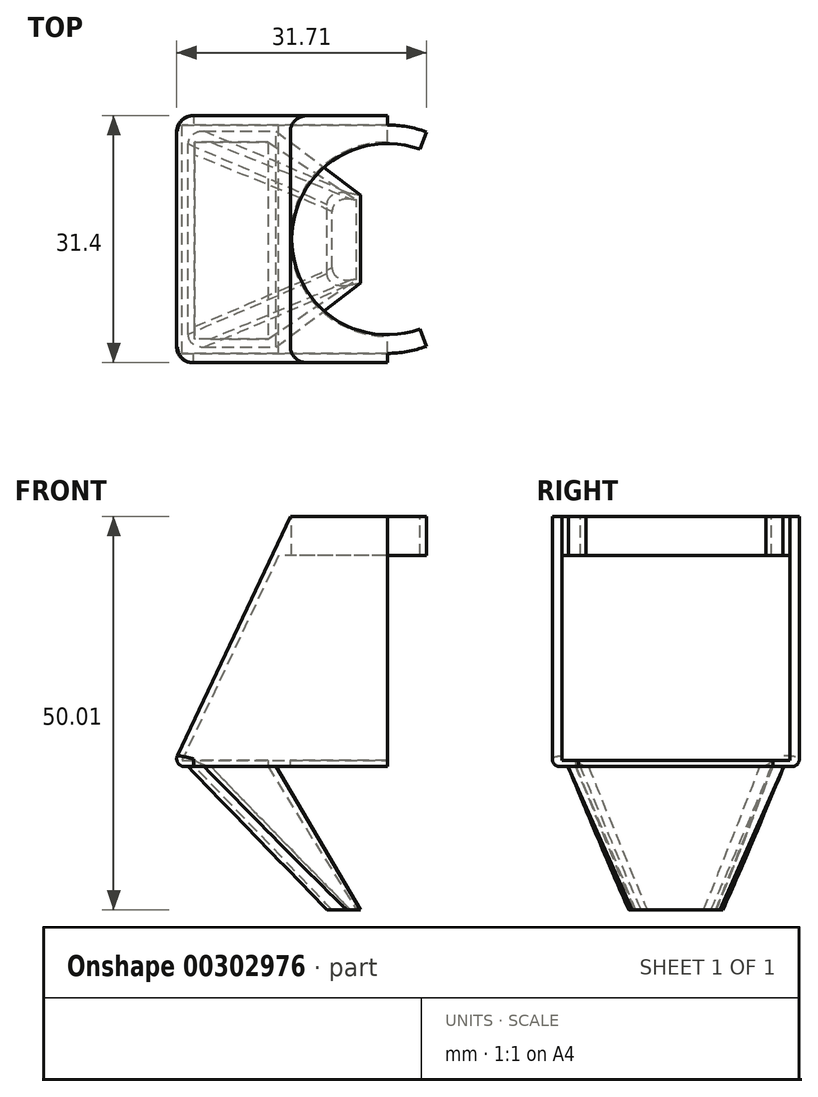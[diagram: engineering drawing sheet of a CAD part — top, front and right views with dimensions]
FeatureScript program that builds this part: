
annotation { "Feature Type Name" : "Feature", "Feature Type Description" : "" }
export const myFeature = defineFeature(function(context is Context, id is Id, definition is map)
    precondition{}
    {
        {
            var Q0;
            Q0=qCreatedBy(makeId("Front.planeOp"),FACE);
            var sketch = newSketch(context, id + "F0", { "sketchPlane" : qUnion([Q0])});
            skLineSegment(sketch, "E0.bottom", {"start": v(12.33, 15.9) * mm, "end": v(-12.33, 15.9) * mm, "construction": true});
            skLineSegment(sketch, "E0.top", {"start": v(12.32, -15.9) * mm, "end": v(-12.33, -15.9) * mm, "construction": true});
            skLineSegment(sketch, "E0.left", {"start": v(12.33, 15.9) * mm, "end": v(12.32, -15.9) * mm, "construction": true});
            skLineSegment(sketch, "E0.right", {"start": v(-12.33, 15.9) * mm, "end": v(-12.33, -15.9) * mm, "construction": true});
            skPoint(sketch, "E0.middle", {"position": v(0, 0) * mm});
            skLineSegment(sketch, "E1", {"start": v(-12.33, 15.9) * mm, "end": v(-27.33, -15.9) * mm});
            skLineSegment(sketch, "E2", {"start": v(-27.33, -15.9) * mm, "end": v(-12.33, -15.9) * mm});
            skLineSegment(sketch, "E3", {"start": v(-13.8, 10.9) * mm, "end": v(-26.06, -15.1) * mm});
            skLineSegment(sketch, "E4", {"start": v(-12.33, -15.1) * mm, "end": v(-26.06, -15.1) * mm});
            skLineSegment(sketch, "E5", {"start": v(-12.33, 15.9) * mm, "end": v(0, 15.9) * mm});
            skLineSegment(sketch, "E6", {"start": v(0, 15.9) * mm, "end": v(0, 10.9) * mm});
            skLineSegment(sketch, "E7", {"start": v(0, 10.9) * mm, "end": v(-13.8, 10.9) * mm});
            skLineSegment(sketch, "E8", {"start": v(-12.33, -15.1) * mm, "end": v(0, -15.1) * mm});
            skLineSegment(sketch, "E9", {"start": v(0, -15.1) * mm, "end": v(0, -15.9) * mm});
            skLineSegment(sketch, "E10", {"start": v(0, -15.9) * mm, "end": v(-12.33, -15.9) * mm});
            skSolve(sketch);
        }
        {
            var Q0;
            Q0=makeQuery(id+"F0.imprint","IMPRINT",FACE,{"disambiguationData":[TD([[makeQuery(id+"F0.imprint","IMPRINT",EDGE,{"derivedFrom":sQuery(id+"F0.wireOp",EDGE,"E1")}),1.0]])]});
            extrude(context, id + "F1", {"entities" : qUnion([Q0]), "endBound" : BoundingType.SYMMETRIC, "depth" : 29 * mm, "offsetDistance" : 25 * mm});
        }
        {
            var Q0;
            Q0=makeQuery(id+"F1.opExtrude","SWEPT_FACE",FACE,{"disambiguationData":[OSD([sQuery(id+"F0.wireOp",EDGE,"E5")])]});
            var sketch = newSketch(context, id + "F2", { "sketchPlane" : qUnion([Q0])});
            skCircle(sketch, "E11", {"center": v(0, 0) * mm, "radius": 12.15 * mm});
            skCircle(sketch, "E12", {"center": v(0, 0) * mm, "radius": 14.5 * mm});
            skLineSegment(sketch, "E13", {"start": v(0, 0) * mm, "end": v(4.96, 13.63) * mm});
            skLineSegment(sketch, "E14", {"start": v(0, 0) * mm, "end": v(4.96, -13.63) * mm});
            skSolve(sketch);
        }
        {
            var Q0;
            {var subQ0=sQuery(id+"F0.wireOp",EDGE,"E5");var subQ1=makeQuery(id+"F1.opExtrude","SWEPT_EDGE",EDGE,{"disambiguationData":[OSD([subQ0,sQuery(id+"F0.wireOp",EDGE,"E6")])]});var subQ3=sQuery(id+"F2.wireOp",EDGE,"E11");var subQ4=makeQuery(id+"F2.imprint","INTERSECT",VERTEX,{"disambiguationData":[OD(0.0)],"derivedFrom":[subQ1,subQ3]});Q0=makeQuery(id+"F2.imprint","IMPRINT",FACE,{"disambiguationData":[TD([[makeQuery(id+"F2.imprint","IMPRINT",EDGE,{"disambiguationData":[TD([[subQ4,-1.0]])],"derivedFrom":subQ3}),1.0]])]});}
            extrude(context, id + "F3", {"entities" : qUnion([Q0]), "operationType" : NewBodyOperationType.REMOVE, "oppositeDirection" : true, "depth" : 6 * mm, "offsetDistance" : 25 * mm});
        }
        {
            var Q0;
            {var subQ0=sQuery(id+"F2.wireOp",EDGE,"E13");var subQ6=sQuery(id+"F2.wireOp",EDGE,"E12");var subQ8=makeQuery(id+"F2.imprint","INTERSECT",VERTEX,{"derivedFrom":[subQ6,subQ0]});Q0=makeQuery(id+"F2.imprint","IMPRINT",FACE,{"disambiguationData":[TD([[makeQuery(id+"F2.imprint","IMPRINT",EDGE,{"disambiguationData":[TD([[subQ8,1.0]])],"derivedFrom":subQ0}),1.0]])]});}
            var Q1;
            {var subQ0=sQuery(id+"F2.wireOp",EDGE,"E14");var subQ6=sQuery(id+"F2.wireOp",EDGE,"E12");var subQ8=makeQuery(id+"F2.imprint","INTERSECT",VERTEX,{"derivedFrom":[subQ6,subQ0]});Q1=makeQuery(id+"F2.imprint","IMPRINT",FACE,{"disambiguationData":[TD([[makeQuery(id+"F2.imprint","IMPRINT",EDGE,{"disambiguationData":[TD([[subQ8,1.0]])],"derivedFrom":subQ0}),-1.0]])]});}
            extrude(context, id + "F4", {"entities" : qUnion([Q0, Q1]), "operationType" : NewBodyOperationType.ADD, "oppositeDirection" : true, "depth" : 5 * mm, "offsetDistance" : 25 * mm});
        }
        {
            var Q0;
            Q0=makeQuery(id+"F1.opExtrude","CAP_FACE",FACE,{"disambiguationData":[OSD([sQuery(id+"F0.wireOp",EDGE,"E1"),sQuery(id+"F0.wireOp",EDGE,"E2"),sQuery(id+"F0.wireOp",EDGE,"E3"),sQuery(id+"F0.wireOp",EDGE,"E4"),sQuery(id+"F0.wireOp",EDGE,"E5"),sQuery(id+"F0.wireOp",EDGE,"E6"),sQuery(id+"F0.wireOp",EDGE,"E7"),sQuery(id+"F0.wireOp",EDGE,"E8"),sQuery(id+"F0.wireOp",EDGE,"E9"),sQuery(id+"F0.wireOp",EDGE,"E10")])],"isStart":false});
            var sketch = newSketch(context, id + "F5", { "sketchPlane" : qUnion([Q0])});
            skLineSegment(sketch, "E15", {"start": v(0, 15.9) * mm, "end": v(0, -15.9) * mm});
            skSolve(sketch);
        }
        {
            var Q0;
            Q0=makeQuery(id+"F5.imprint","IMPRINT",FACE,{"disambiguationData":[TD([[makeQuery(id+"F5.imprint","IMPRINT",EDGE,{"derivedFrom":makeQuery(id+"F1.opExtrude","CAP_EDGE",EDGE,{"disambiguationData":[OSD([sQuery(id+"F0.wireOp",EDGE,"E1")])],"isStart":false})}),1.0]])]});
            var Q1;
            Q1=makeQuery(id+"F5.imprint","IMPRINT",FACE,{"disambiguationData":[TD([[makeQuery(id+"F5.imprint","IMPRINT",EDGE,{"derivedFrom":makeQuery(id+"F1.opExtrude","CAP_EDGE",EDGE,{"disambiguationData":[OSD([sQuery(id+"F0.wireOp",EDGE,"E3")])],"isStart":false})}),1.0]])]});
            extrude(context, id + "F6", {"entities" : qUnion([Q0, Q1]), "operationType" : NewBodyOperationType.ADD, "depth" : 1.2 * mm, "offsetDistance" : 25 * mm});
        }
        {
            var Q0;
            Q0=makeQuery(id+"F1.opExtrude","CAP_FACE",FACE,{"disambiguationData":[OSD([sQuery(id+"F0.wireOp",EDGE,"E1"),sQuery(id+"F0.wireOp",EDGE,"E2"),sQuery(id+"F0.wireOp",EDGE,"E3"),sQuery(id+"F0.wireOp",EDGE,"E4"),sQuery(id+"F0.wireOp",EDGE,"E5"),sQuery(id+"F0.wireOp",EDGE,"E6"),sQuery(id+"F0.wireOp",EDGE,"E7"),sQuery(id+"F0.wireOp",EDGE,"E8"),sQuery(id+"F0.wireOp",EDGE,"E9"),sQuery(id+"F0.wireOp",EDGE,"E10")])],"isStart":true});
            var sketch = newSketch(context, id + "F7", { "sketchPlane" : qUnion([Q0])});
            skLineSegment(sketch, "E16", {"start": v(0, 15.9) * mm, "end": v(0, -15.9) * mm});
            skSolve(sketch);
        }
        {
            var Q0;
            Q0=makeQuery(id+"F7.imprint","IMPRINT",FACE,{"disambiguationData":[TD([[makeQuery(id+"F7.imprint","IMPRINT",EDGE,{"derivedFrom":makeQuery(id+"F1.opExtrude","CAP_EDGE",EDGE,{"disambiguationData":[OSD([sQuery(id+"F0.wireOp",EDGE,"E1")])],"isStart":true})}),-1.0]])]});
            var Q1;
            Q1=makeQuery(id+"F7.imprint","IMPRINT",FACE,{"disambiguationData":[TD([[makeQuery(id+"F7.imprint","IMPRINT",EDGE,{"derivedFrom":makeQuery(id+"F1.opExtrude","CAP_EDGE",EDGE,{"disambiguationData":[OSD([sQuery(id+"F0.wireOp",EDGE,"E3")])],"isStart":true})}),-1.0]])]});
            extrude(context, id + "F8", {"entities" : qUnion([Q0, Q1]), "operationType" : NewBodyOperationType.ADD, "depth" : 1.2 * mm, "offsetDistance" : 25 * mm});
        }
        {
            var Q0;
            {var subQ0=sQuery(id+"F0.wireOp",EDGE,"E10");var subQ1=sQuery(id+"F0.wireOp",EDGE,"E2");Q0=makeQuery(id+"F8.boolean.opBoolean","MERGE",FACE,{"derivedFrom":[makeQuery(id+"F6.boolean.opBoolean","MERGE",FACE,{"derivedFrom":[makeQuery(id+"F1.opExtrude","SWEPT_FACE",FACE,{"disambiguationData":[OSD([subQ1,subQ0])]}),makeQuery(id+"F6.opExtrude","SWEPT_FACE",FACE,{"disambiguationData":[OSD([subQ1,subQ0])]})]}),makeQuery(id+"F8.opExtrude","SWEPT_FACE",FACE,{"disambiguationData":[OSD([subQ1,subQ0])]})]});}
            var sketch = newSketch(context, id + "F9", { "sketchPlane" : qUnion([Q0])});
            skCircle(sketch, "E17", {"center": v(0, 0) * mm, "radius": 12.35 * mm});
            skSolve(sketch);
        }
        {
            var Q0;
            {var subQ0=sQuery(id+"F9.wireOp",EDGE,"E17");var subQ1=sQuery(id+"F0.wireOp",EDGE,"E10");var subQ2=sQuery(id+"F0.wireOp",EDGE,"E2");var subQ3=makeQuery(id+"F8.boolean.opBoolean","MERGE",EDGE,{"derivedFrom":[makeQuery(id+"F6.boolean.opBoolean","MERGE",EDGE,{"derivedFrom":[makeQuery(id+"F1.opExtrude","SWEPT_EDGE",EDGE,{"disambiguationData":[OSD([sQuery(id+"F0.wireOp",EDGE,"E9"),subQ1])]}),makeQuery(id+"F6.opExtrude","SWEPT_EDGE",EDGE,{"disambiguationData":[OSD([subQ2,subQ1,sQuery(id+"F5.wireOp",EDGE,"E15")])]})]}),makeQuery(id+"F8.opExtrude","SWEPT_EDGE",EDGE,{"disambiguationData":[OSD([subQ2,subQ1,sQuery(id+"F7.wireOp",EDGE,"E16")])]})]});var subQ4=makeQuery(id+"F9.imprint","INTERSECT",VERTEX,{"disambiguationData":[OD(0.0)],"derivedFrom":[subQ3,subQ0]});Q0=makeQuery(id+"F9.imprint","IMPRINT",FACE,{"disambiguationData":[TD([[makeQuery(id+"F9.imprint","IMPRINT",EDGE,{"disambiguationData":[TD([[subQ4,-1.0]])],"derivedFrom":subQ0}),1.0]])]});}
            extrude(context, id + "F10", {"entities" : qUnion([Q0]), "operationType" : NewBodyOperationType.REMOVE, "oppositeDirection" : true, "depth" : 2 * mm, "offsetDistance" : 25 * mm});
        }
        {
            var Q0;
            {var subQ0=sQuery(id+"F0.wireOp",EDGE,"E10");var subQ1=sQuery(id+"F0.wireOp",EDGE,"E2");Q0=makeQuery(id+"F8.boolean.opBoolean","MERGE",FACE,{"derivedFrom":[makeQuery(id+"F6.boolean.opBoolean","MERGE",FACE,{"derivedFrom":[makeQuery(id+"F1.opExtrude","SWEPT_FACE",FACE,{"disambiguationData":[OSD([subQ1,subQ0])]}),makeQuery(id+"F6.opExtrude","SWEPT_FACE",FACE,{"disambiguationData":[OSD([subQ1,subQ0])]})]}),makeQuery(id+"F8.opExtrude","SWEPT_FACE",FACE,{"disambiguationData":[OSD([subQ1,subQ0])]})]});}
            var sketch = newSketch(context, id + "F11", { "sketchPlane" : qUnion([Q0])});
            skLineSegment(sketch, "E18.bottom", {"start": v(-25.32, 13.7) * mm, "end": v(-14.15, 13.7) * mm});
            skLineSegment(sketch, "E18.top", {"start": v(-25.32, -13.7) * mm, "end": v(-14.15, -13.7) * mm});
            skLineSegment(sketch, "E18.left", {"start": v(-25.32, 13.7) * mm, "end": v(-25.32, -13.7) * mm});
            skLineSegment(sketch, "E18.right", {"start": v(-14.15, 13.7) * mm, "end": v(-14.15, -13.7) * mm});
            skSolve(sketch);
        }
        {
            var Q0;
            Q0=makeQuery(id+"F11.imprint","IMPRINT",FACE,{"disambiguationData":[TD([[makeQuery(id+"F11.imprint","IMPRINT",EDGE,{"derivedFrom":sQuery(id+"F11.wireOp",EDGE,"E18.bottom")}),1.0]])]});
            var sketch = newSketch(context, id + "F12", { "sketchPlane" : qUnion([Q0])});
            skLineSegment(sketch, "E19.bottom", {"start": v(-24.47, 12.69) * mm, "end": v(-15.17, 12.69) * mm});
            skLineSegment(sketch, "E19.top", {"start": v(-24.47, -12.3) * mm, "end": v(-15.17, -12.3) * mm});
            skLineSegment(sketch, "E19.left", {"start": v(-24.47, 12.69) * mm, "end": v(-24.47, -12.3) * mm});
            skLineSegment(sketch, "E19.right", {"start": v(-15.17, 12.69) * mm, "end": v(-15.17, -12.3) * mm});
            skSolve(sketch);
        }
        {
            var Q0;
            Q0=makeQuery(id+"F12.imprint","IMPRINT",FACE,{"disambiguationData":[TD([[makeQuery(id+"F12.imprint","IMPRINT",EDGE,{"derivedFrom":sQuery(id+"F12.wireOp",EDGE,"E19.bottom")}),-1.0]])]});
            extrude(context, id + "F13", {"entities" : qUnion([Q0]), "operationType" : NewBodyOperationType.REMOVE, "oppositeDirection" : true, "depth" : 2 * mm, "offsetDistance" : 25 * mm});
        }
        {
            var Q0;
            {var subQ0=sQuery(id+"F5.wireOp",EDGE,"E15");var subQ2=sQuery(id+"F0.wireOp",EDGE,"E5");Q0=makeQuery(id+"F10.boolean.opBoolean","SPLIT",FACE,{"disambiguationData":[TD([makeQuery(id+"F6.opExtrude","SWEPT_FACE",FACE,{"disambiguationData":[OSD([subQ2])]})])],"derivedFrom":makeQuery(id+"F8.boolean.opBoolean","MERGE",FACE,{"derivedFrom":[makeQuery(id+"F6.boolean.opBoolean","MERGE",FACE,{"derivedFrom":[makeQuery(id+"F1.opExtrude","SWEPT_FACE",FACE,{"disambiguationData":[OSD([sQuery(id+"F0.wireOp",EDGE,"E9")])]}),makeQuery(id+"F6.opExtrude","SWEPT_FACE",FACE,{"disambiguationData":[OSD([subQ0])]})]}),makeQuery(id+"F8.opExtrude","SWEPT_FACE",FACE,{"disambiguationData":[OSD([sQuery(id+"F7.wireOp",EDGE,"E16")])]})]})});}
            var sketch = newSketch(context, id + "F14", { "sketchPlane" : qUnion([Q0])});
            skLineSegment(sketch, "E20", {"start": v(-15.7, -15.9) * mm, "end": v(0, -15.9) * mm, "construction": true});
            skLineSegment(sketch, "E21", {"start": v(0, -15.9) * mm, "end": v(0, 0) * mm, "construction": true});
            skLineSegment(sketch, "E22", {"start": v(0, -15.9) * mm, "end": v(0, -40.9) * mm, "construction": true});
            skLineSegment(sketch, "E23.bottom", {"start": v(2.5, -40.4) * mm, "end": v(-2.5, -40.4) * mm});
            skLineSegment(sketch, "E23.top", {"start": v(2.5, -41.4) * mm, "end": v(-2.5, -41.4) * mm});
            skLineSegment(sketch, "E23.left", {"start": v(2.5, -40.4) * mm, "end": v(2.5, -41.4) * mm});
            skLineSegment(sketch, "E23.right", {"start": v(-2.5, -40.4) * mm, "end": v(-2.5, -41.4) * mm});
            skPoint(sketch, "E23.middle", {"position": v(0, -40.9) * mm});
            skSolve(sketch);
        }
        {
            var Q0;
            {var subQ0=sQuery(id+"F7.wireOp",EDGE,"E16");var subQ2=sQuery(id+"F0.wireOp",EDGE,"E5");Q0=makeQuery(id+"F10.boolean.opBoolean","SPLIT",FACE,{"disambiguationData":[TD([makeQuery(id+"F8.opExtrude","SWEPT_FACE",FACE,{"disambiguationData":[OSD([subQ2])]})])],"derivedFrom":makeQuery(id+"F8.boolean.opBoolean","MERGE",FACE,{"derivedFrom":[makeQuery(id+"F6.boolean.opBoolean","MERGE",FACE,{"derivedFrom":[makeQuery(id+"F1.opExtrude","SWEPT_FACE",FACE,{"disambiguationData":[OSD([sQuery(id+"F0.wireOp",EDGE,"E9")])]}),makeQuery(id+"F6.opExtrude","SWEPT_FACE",FACE,{"disambiguationData":[OSD([sQuery(id+"F5.wireOp",EDGE,"E15")])]})]}),makeQuery(id+"F8.opExtrude","SWEPT_FACE",FACE,{"disambiguationData":[OSD([subQ0])]})]})});}
            var sketch = newSketch(context, id + "F15", { "sketchPlane" : qUnion([Q0])});
            skLineSegment(sketch, "E24", {"start": v(15.7, -15.9) * mm, "end": v(0, -15.9) * mm, "construction": true});
            skLineSegment(sketch, "E25", {"start": v(0, -15.9) * mm, "end": v(0, 0) * mm, "construction": true});
            skLineSegment(sketch, "E26", {"start": v(0, -15.9) * mm, "end": v(0, -40.9) * mm, "construction": true});
            skLineSegment(sketch, "E27.bottom", {"start": v(-3.06, -39.8) * mm, "end": v(3.06, -39.8) * mm});
            skLineSegment(sketch, "E27.top", {"start": v(-3.06, -42) * mm, "end": v(3.06, -42) * mm});
            skLineSegment(sketch, "E27.left", {"start": v(-3.06, -39.8) * mm, "end": v(-3.06, -42) * mm});
            skLineSegment(sketch, "E27.right", {"start": v(3.06, -39.8) * mm, "end": v(3.06, -42) * mm});
            skPoint(sketch, "E27.middle", {"position": v(0, -40.9) * mm});
            skSolve(sketch);
        }
        {
            var Q1;
            Q1=makeQuery(id+"F11.imprint","IMPRINT",FACE,{"disambiguationData":[TD([[makeQuery(id+"F11.imprint","IMPRINT",EDGE,{"derivedFrom":sQuery(id+"F11.wireOp",EDGE,"E18.bottom")}),-1.0]])]});
            var Q2;
            Q2=makeQuery(id+"F15.imprint","IMPRINT",FACE,{"disambiguationData":[TD([[makeQuery(id+"F15.imprint","IMPRINT",EDGE,{"derivedFrom":sQuery(id+"F15.wireOp",EDGE,"E27.bottom")}),-1.0]])]});
            loft(context, id + "F16", {"operationType" : NewBodyOperationType.ADD, "sheetProfilesArray" : [{ "sheetProfileEntities" : qUnion([Q1]) }, { "sheetProfileEntities" : qUnion([Q2]) }]});
        }
        {
            var Q0;
            Q0 = qSketchRegion(id + "F12", true);
            var Q1;
            Q1 = qSketchRegion(id + "F14", true);
            loft(context, id + "F17", {"operationType" : NewBodyOperationType.REMOVE, "sheetProfilesArray" : [{ "sheetProfileEntities" : qUnion([Q0]) }, { "sheetProfileEntities" : qUnion([Q1]) }]});
        }
        {
            var Q0;
            Q0=qCreatedBy(makeId("Front.planeOp"),FACE);
            var sketch = newSketch(context, id + "F18", { "sketchPlane" : qUnion([Q0])});
            skLineSegment(sketch, "E28.bottom", {"start": v(0, -81.29) * mm, "end": v(-13.07, -81.29) * mm});
            skLineSegment(sketch, "E28.top", {"start": v(0, -71.29) * mm, "end": v(-13.07, -71.29) * mm});
            skLineSegment(sketch, "E28.left", {"start": v(0, -81.29) * mm, "end": v(0, -71.29) * mm});
            skLineSegment(sketch, "E28.right", {"start": v(-13.07, -81.29) * mm, "end": v(-13.07, -71.29) * mm});
            skLineSegment(sketch, "E29.bottom", {"start": v(-25.88, -47.1) * mm, "end": v(5.48, -47.1) * mm});
            skLineSegment(sketch, "E29.top", {"start": v(-25.88, -34.1) * mm, "end": v(5.48, -34.1) * mm});
            skLineSegment(sketch, "E29.left", {"start": v(-25.88, -47.1) * mm, "end": v(-25.88, -34.1) * mm});
            skLineSegment(sketch, "E29.right", {"start": v(5.48, -47.1) * mm, "end": v(5.48, -34.1) * mm});
            skSolve(sketch);
        }
        {
            var Q0;
            Q0=makeQuery(id+"F18.imprint","IMPRINT",FACE,{"disambiguationData":[TD([[makeQuery(id+"F18.imprint","IMPRINT",EDGE,{"derivedFrom":sQuery(id+"F18.wireOp",EDGE,"E29.bottom")}),1.0]])]});
            extrude(context, id + "F19", {"entities" : qUnion([Q0]), "operationType" : NewBodyOperationType.REMOVE, "endBound" : BoundingType.SYMMETRIC, "depth" : 25 * mm, "offsetDistance" : 25 * mm});
        }
        {
            var Q0;
            Q0=makeQuery(id+"F1.opExtrude","CAP_EDGE",EDGE,{"disambiguationData":[OSD([sQuery(id+"F0.wireOp",EDGE,"E3")])],"isStart":false});
            var Q1;
            Q1=makeQuery(id+"F1.opExtrude","CAP_EDGE",EDGE,{"disambiguationData":[OSD([sQuery(id+"F0.wireOp",EDGE,"E3")])],"isStart":true});
            var Q2;
            Q2=makeQuery(id+"F6.opExtrude","CAP_EDGE",EDGE,{"disambiguationData":[OSD([sQuery(id+"F0.wireOp",EDGE,"E1")])],"isStart":false});
            var Q3;
            Q3=makeQuery(id+"F8.opExtrude","CAP_EDGE",EDGE,{"disambiguationData":[OSD([sQuery(id+"F0.wireOp",EDGE,"E1")])],"isStart":false});
            fillet(context, id + "F20", {"entities" : qUnion([Q0, Q1, Q2, Q3]), "radius" : 2 * mm, "tangentPropagation" : true, "allowEdgeOverflow" : false});
        }
        {
            var Q0;
            Q0=makeQuery(id+"F8.opExtrude","CAP_EDGE",EDGE,{"disambiguationData":[OSD([sQuery(id+"F0.wireOp",EDGE,"E2"),sQuery(id+"F0.wireOp",EDGE,"E10")])],"isStart":false});
            var Q1;
            Q1=makeQuery(id+"F20.opFillet","BLEND_EDGE",EDGE,{"blendedFrom":[makeQuery(id+"F1.opExtrude","CAP_EDGE",EDGE,{"disambiguationData":[OSD([sQuery(id+"F0.wireOp",EDGE,"E3")])],"isStart":true}),makeQuery(id+"F1.opExtrude","SWEPT_FACE",FACE,{"disambiguationData":[OSD([sQuery(id+"F0.wireOp",EDGE,"E4"),sQuery(id+"F0.wireOp",EDGE,"E8")])]})],"blendedInto":[makeQuery(id+"F1.opExtrude","SWEPT_FACE",FACE,{"disambiguationData":[OSD([sQuery(id+"F0.wireOp",EDGE,"E4"),sQuery(id+"F0.wireOp",EDGE,"E8")])]})]});
            fillet(context, id + "F21", {"entities" : qUnion([Q0, Q1]), "radius" : 1 * mm, "tangentPropagation" : true, "allowEdgeOverflow" : false});
        }
        {
            var Q0;
            Q0=makeQuery(id+"F17.boolean.opBoolean","COPY",EDGE,{"derivedFrom":makeQuery(id+"F17.opLoft","SWEPT_EDGE",EDGE,{"disambiguationData":[OSD([sQuery(id+"F12.wireOp",EDGE,"E19.bottom"),sQuery(id+"F12.wireOp",EDGE,"E19.left"),sQuery(id+"F14.wireOp",EDGE,"E23.top"),sQuery(id+"F14.wireOp",EDGE,"E23.right")])]})});
            var Q1;
            Q1=makeQuery(id+"F17.boolean.opBoolean","COPY",EDGE,{"derivedFrom":makeQuery(id+"F17.opLoft","SWEPT_EDGE",EDGE,{"disambiguationData":[OSD([sQuery(id+"F12.wireOp",EDGE,"E19.top"),sQuery(id+"F12.wireOp",EDGE,"E19.left"),sQuery(id+"F14.wireOp",EDGE,"E23.top"),sQuery(id+"F14.wireOp",EDGE,"E23.left")])]})});
            var Q2;
            Q2=makeQuery(id+"F16.opLoft","SWEPT_EDGE",EDGE,{"disambiguationData":[OSD([sQuery(id+"F11.wireOp",EDGE,"E18.bottom"),sQuery(id+"F11.wireOp",EDGE,"E18.left"),sQuery(id+"F15.wireOp",EDGE,"E27.top"),sQuery(id+"F15.wireOp",EDGE,"E27.left")])]});
            var Q3;
            Q3=makeQuery(id+"F16.opLoft","SWEPT_EDGE",EDGE,{"disambiguationData":[OSD([sQuery(id+"F11.wireOp",EDGE,"E18.top"),sQuery(id+"F11.wireOp",EDGE,"E18.left"),sQuery(id+"F15.wireOp",EDGE,"E27.top"),sQuery(id+"F15.wireOp",EDGE,"E27.right")])]});
            fillet(context, id + "F22", {"entities" : qUnion([Q0, Q1, Q2, Q3]), "radius" : 2 * mm, "tangentPropagation" : true, "allowEdgeOverflow" : false});
        }
    });
